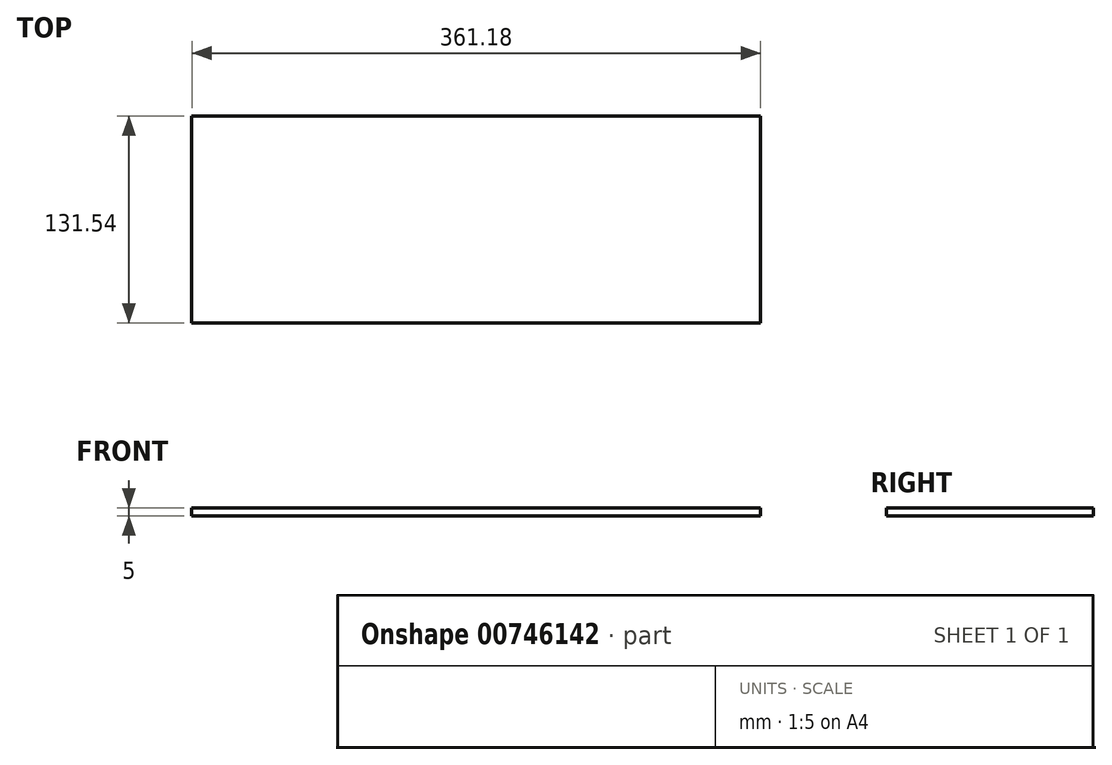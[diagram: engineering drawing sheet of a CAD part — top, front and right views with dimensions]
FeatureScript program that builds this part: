
annotation { "Feature Type Name" : "Feature", "Feature Type Description" : "" }
export const myFeature = defineFeature(function(context is Context, id is Id, definition is map)
    precondition{}
    {
        {
            var Q0;
            Q0=qCreatedBy(makeId("Top.planeOp"),FACE);
            var sketch = newSketch(context, id + "F0", { "sketchPlane" : qUnion([Q0])});
            skLineSegment(sketch, "E0.bottom", {"start": v(-180.6, -65.77) * mm, "end": v(180.6, -65.77) * mm});
            skLineSegment(sketch, "E0.top", {"start": v(-180.6, 65.77) * mm, "end": v(180.6, 65.77) * mm});
            skLineSegment(sketch, "E0.left", {"start": v(-180.6, -65.77) * mm, "end": v(-180.6, 65.77) * mm});
            skLineSegment(sketch, "E0.right", {"start": v(180.6, -65.77) * mm, "end": v(180.6, 65.77) * mm});
            skPoint(sketch, "E0.middle", {"position": v(0, 0) * mm});
            skSolve(sketch);
        }
        {
            var Q0;
            Q0=makeQuery(id+"F0.imprint","IMPRINT",FACE,{"disambiguationData":[TD([[makeQuery(id+"F0.imprint","IMPRINT",EDGE,{"derivedFrom":sQuery(id+"F0.wireOp",EDGE,"E0.bottom")}),1.0]])]});
            extrude(context, id + "F1", {"entities" : qUnion([Q0]), "depth" : 5 * mm, "offsetDistance" : 25 * mm});
        }
    });
